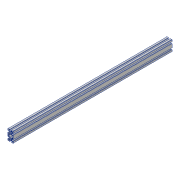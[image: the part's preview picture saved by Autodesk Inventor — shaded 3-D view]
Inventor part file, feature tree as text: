
AUTODESK INVENTOR PART (.ipt)
format: ipt  version: 2018 (Build 220112000, 112)  size: 240,640 bytes
history: native  units: mm
features: extrude x1, sketch x1
ambient origin geometry x8: Origin, YZ Plane, XZ Plane, XY Plane, X Axis, Y Axis, Z Axis, Center Point
bodies: Solid1 (feature_tree)
feature tree (2):
  extrude  "Extrusion1"  [1 undecoded]
  sketch  "Sketch1"  dims[d0=600.0mm d1=0.0mm]
note: 1 required parameter value undecoded (feature->parameter linkage not recoverable at this tier; creation-order binding heuristic only, values carry confidence <= 0.55)
